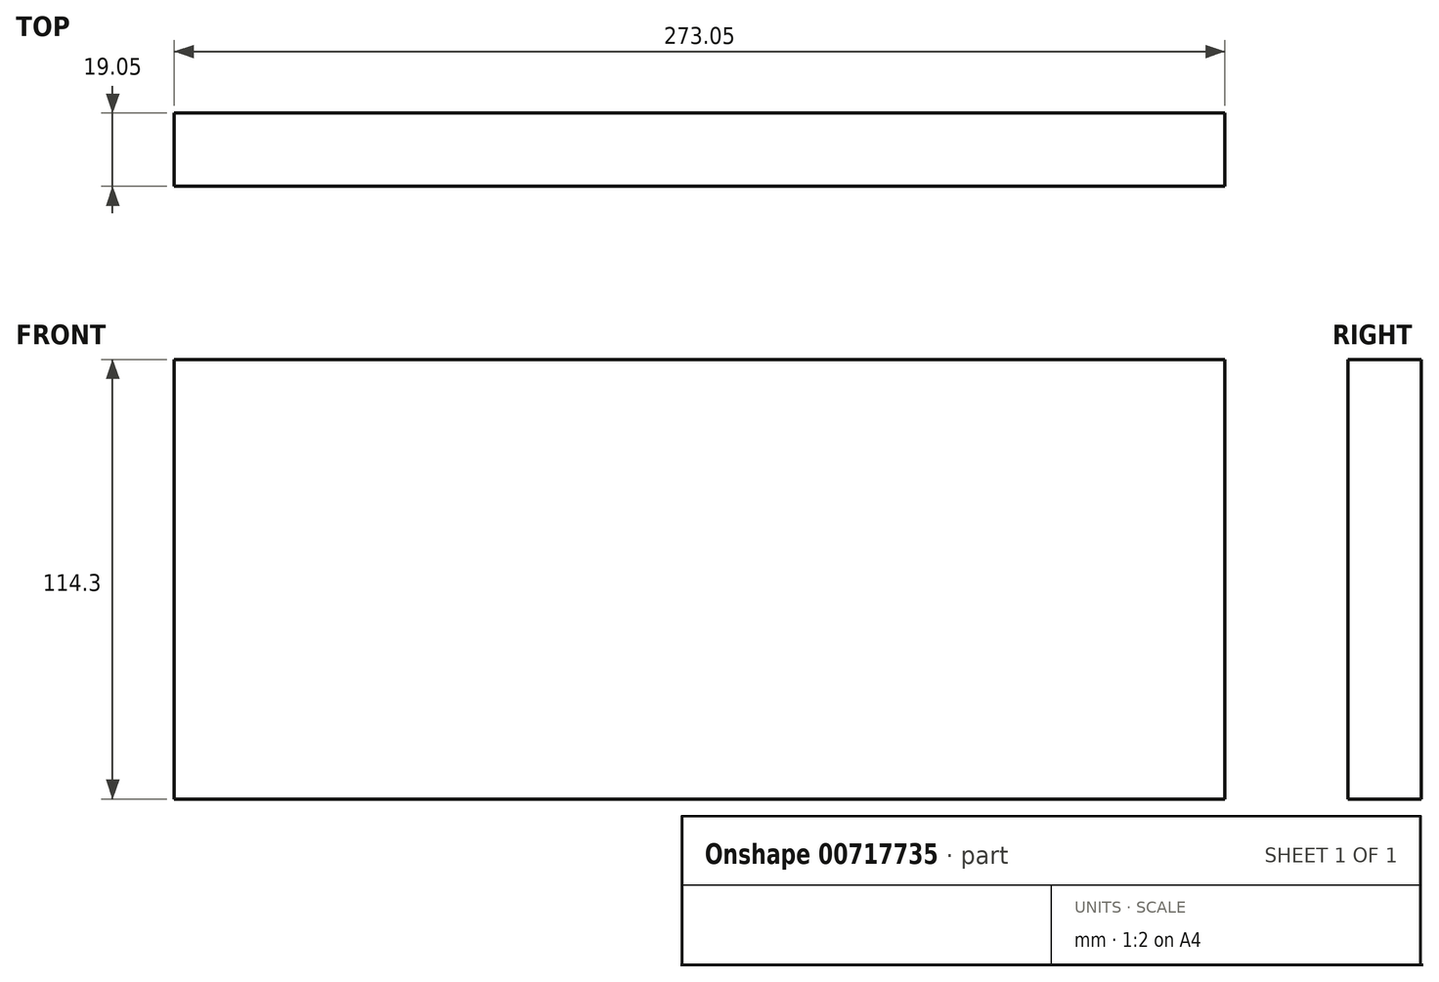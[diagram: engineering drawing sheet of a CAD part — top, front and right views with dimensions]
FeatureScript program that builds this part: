
annotation { "Feature Type Name" : "Feature", "Feature Type Description" : "" }
export const myFeature = defineFeature(function(context is Context, id is Id, definition is map)
    precondition{}
    {
        {
            var Q0;
            Q0=qCreatedBy(makeId("Front.planeOp"),FACE);
            var sketch = newSketch(context, id + "F0", { "sketchPlane" : qUnion([Q0])});
            skLineSegment(sketch, "E0.bottom", {"start": v(-129.65, 64.71) * mm, "end": v(143.4, 64.71) * mm});
            skLineSegment(sketch, "E0.top", {"start": v(-129.65, -49.59) * mm, "end": v(143.4, -49.59) * mm});
            skLineSegment(sketch, "E0.left", {"start": v(-129.65, 64.71) * mm, "end": v(-129.65, -49.59) * mm});
            skLineSegment(sketch, "E0.right", {"start": v(143.4, 64.71) * mm, "end": v(143.4, -49.59) * mm});
            skSolve(sketch);
        }
        {
            var Q0;
            Q0 = qSketchRegion(id + "F0", true);
            extrude(context, id + "F1", {"entities" : qUnion([Q0]), "depth" : 19.05 * mm, "offsetDistance" : 25.4 * mm});
        }
    });
